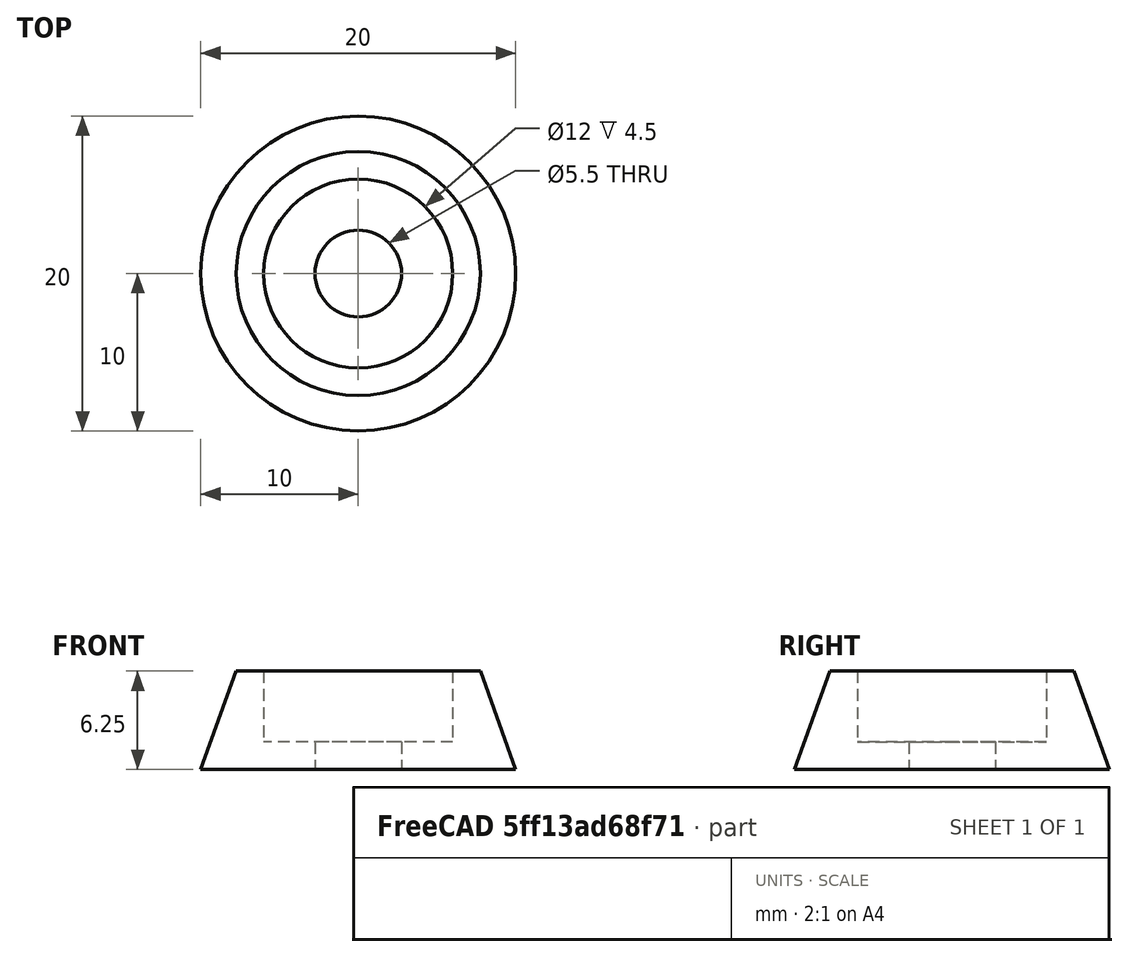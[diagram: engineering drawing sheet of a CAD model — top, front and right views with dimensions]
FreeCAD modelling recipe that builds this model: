
FCSTD DOCUMENT  (FreeCAD 0.17R13662 (Git))
Label: frame_foot
License: CreativeCommons Attribution-ShareAlike
LicenseURL: http://creativecommons.org/licenses/by-sa/4.0/
objects: Sketcher::SketchObject×1, PartDesign::Revolution×1, PartDesign::Body×1
note: 4 computed .brp shape members not serialized (recipe doc carries the construction recipe); baked Part::Feature solids carry a one-line shape summary decoded from their .brp

FEATURE [Sketcher::SketchObject] Sketch
  MapMode = 5
  Placement = pos=(0,0,0) rot=(1,0,0;1.5708rad)
  Support = -> [XZ_Plane]
  sketch-geometry (6):
    g0: LineSegment StartX=6 StartY=6.25 StartZ=0 EndX=6 EndY=1.75 EndZ=0
    g1: LineSegment StartX=6 StartY=1.75 StartZ=0 EndX=2.75 EndY=1.75 EndZ=0
    g2: LineSegment StartX=2.75 StartY=1.75 StartZ=0 EndX=2.75 EndY=0 EndZ=0
    g3: LineSegment StartX=2.75 StartY=0 StartZ=0 EndX=10 EndY=0 EndZ=0
    g4: LineSegment StartX=10 StartY=0 StartZ=0 EndX=7.75 EndY=6.25 EndZ=0
    g5: LineSegment StartX=7.75 StartY=6.25 StartZ=0 EndX=6 EndY=6.25 EndZ=0
  constraints (18):
    c: Coincident(g0,g1)
    c: Coincident(g1,g2)
    c: Coincident(g2,g3)
    c: Coincident(g3,g4)
    c: Coincident(g4,g5)
    c: Coincident(g0,g5)
    c: Horizontal(g3)
    c: Horizontal(g1)
    c: Horizontal(g5)
    c: Vertical(g2)
    c: Vertical(g0)
    c: PointOnObject(g2,g-1)
    c: DistanceX(g3) = 10
    c: DistanceX(g2) = 2.75
    c: DistanceY(g2,g2) = 1.75
    c: DistanceX(g1,g1) = 3.25
    c: DistanceY(g0,g0) = 4.5
    c: DistanceX(g5,g5) = 1.75
FEATURE [PartDesign::Revolution] Revolution
  Angle = 360
  Axis = (0,0,1)
  Base = (0,0,0)
  Placement = pos=(0,0,0) rot=(1,0,0;1.5708rad)
  Profile = -> Sketch
  ReferenceAxis = -> Sketch [V_Axis]
  Reversed = true
FEATURE [PartDesign::Body] Body
  Group = -> [Sketch,Revolution]
  Origin = -> Origin
  Tip = -> Revolution
